# Revit family: PURELIGHT-RA238-DAWSxxx
name_source: partatom
category: Oprawy oświetleniowe
units: mm (PartAtom-declared; Revit-internal decimal feet)

## family parameters
Numer OmniClass = 23.80.70.11
Obiekt nadrzędny = Powierzchnia
Punkt obliczania pomieszczeń = Nie
Tnij formami wycięć po wczytaniu = Nie
Typ części = Normalny
Tytuł OmniClass = Luminaries for Internal Lighting
Współdzielony = Nie
Wymiar okrągłego złącza = Użyj średnicy
Źródło światła = Tak

## types (3) — shared parameters
Emituj kształt widoczny w renderingu = Nie
Emituj z długości prostokąta = 90 mm  [stored 0.295276 ft]
Emituj z szerokości prostokąta = 2355 mm  [stored 7.72638 ft]
Filtr koloru = 16777215
Kod zespołu = D5020200
Lampa = LED
Obciążenie pozorne = 70 VA
Odchylenie kierunku = 90.00°
Plik sieci fotometrycznej = PURELIGHT-RA149 DAWS840O0650.IES
Producent = RIDI Leuchten GmbH
URL = www.spectral-lighting.com
Zmiana temperatury barwowej przyciemniania lampy = <Brak>
brand = Spectral
conformity mark = CE
electrical safety class = 1
height = 114 mm  [stored 0.374016 ft]
ingress protection (IP) code = IP20
length = 2380 mm  [stored 7.8084 ft]
nominal frequency = 50-60Hz
nominal voltage = 230
rated input power = 70
voltage type (AC, DC, UC) = AC
weight = 9 kg
width = 95 mm
zero-valued in all types: Domyślna rzędna

## per-type parameters (varying)
| type | Model |
| PURELIGHT-RA238 DAWS830O0950 | SPG0630263 |
| PURELIGHT-RA238 DAWS840O1000 | SPG0630264 |
| PURELIGHT-RA238 DAWS8TWO0900 | SPG0630265 |

note: column(s) folded — value = type name in every type: product name

note: [stored X ft] marks values corroborated as IEEE doubles in the binary element streams (Revit-internal decimal feet)
